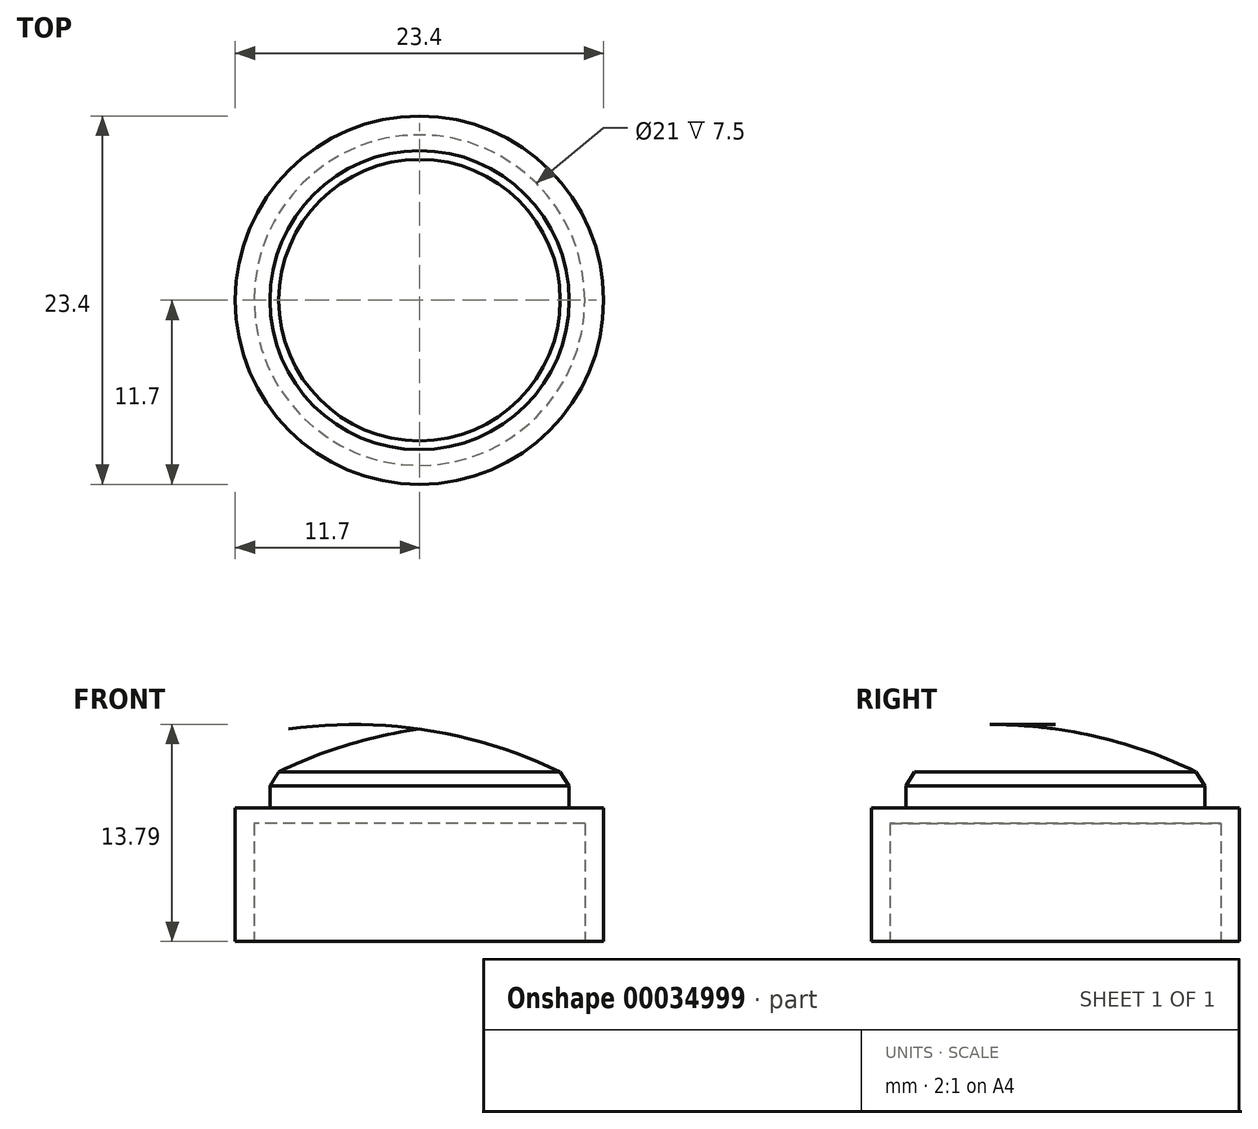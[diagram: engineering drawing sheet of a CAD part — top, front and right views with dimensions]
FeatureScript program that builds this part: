
annotation { "Feature Type Name" : "Feature", "Feature Type Description" : "" }
export const myFeature = defineFeature(function(context is Context, id is Id, definition is map)
    precondition{}
    {
        {
            var Q0;
            Q0=qCreatedBy(makeId("Top.planeOp"),FACE);
            var sketch = newSketch(context, id + "F0", { "sketchPlane" : qUnion([Q0])});
            skCircle(sketch, "E0", {"center": v(0, 0) * mm, "radius": 11.7 * mm});
            skCircle(sketch, "E1", {"center": v(0, 0) * mm, "radius": 10.5 * mm});
            skSolve(sketch);
        }
        {
            var Q0;
            Q0=makeQuery(id+"F0.imprint","IMPRINT",FACE,{"disambiguationData":[TD([[makeQuery(id+"F0.imprint","IMPRINT",EDGE,{"derivedFrom":sQuery(id+"F0.wireOp",EDGE,"E0")}),1.0]])]});
            var Q1;
            Q1=makeQuery(id+"F0.imprint","IMPRINT",FACE,{"disambiguationData":[TD([[makeQuery(id+"F0.imprint","IMPRINT",EDGE,{"derivedFrom":sQuery(id+"F0.wireOp",EDGE,"E1")}),1.0]])]});
            var Q2;
            Q2=sQuery(id+"F0.wireOp",EDGE,"E0");
            extrude(context, id + "F1", {"entities" : qUnion([Q0, Q1]), "surfaceEntities" : qUnion([Q2]), "depth" : 8.5 * mm});
        }
        {
            var Q0;
            Q0=makeQuery(id+"F0.imprint","IMPRINT",FACE,{"disambiguationData":[TD([[makeQuery(id+"F0.imprint","IMPRINT",EDGE,{"derivedFrom":sQuery(id+"F0.wireOp",EDGE,"E1")}),1.0]])]});
            extrude(context, id + "F2", {"entities" : qUnion([Q0]), "operationType" : NewBodyOperationType.REMOVE, "depth" : 7.5 * mm});
        }
        {
            var Q0;
            Q0=makeQuery(id+"F1.opExtrude","CAP_FACE",FACE,{"disambiguationData":[OSD([sQuery(id+"F0.wireOp",EDGE,"E0")])],"isStart":false});
            var sketch = newSketch(context, id + "F3", { "sketchPlane" : qUnion([Q0])});
            skCircle(sketch, "E2", {"center": v(0, 0) * mm, "radius": 9.5 * mm});
            skSolve(sketch);
        }
        {
            var Q0;
            Q0=makeQuery(id+"F3.imprint","IMPRINT",FACE,{"disambiguationData":[TD([[makeQuery(id+"F3.imprint","IMPRINT",EDGE,{"derivedFrom":sQuery(id+"F3.wireOp",EDGE,"b6d1c2b3-00fd-435d-919e-db7ff6a15c5d.0")}),1.0]])]});
            var Q1;
            Q1=makeQuery(id+"F3.imprint","IMPRINT",FACE,{"disambiguationData":[TD([[makeQuery(id+"F3.imprint","IMPRINT",EDGE,{"derivedFrom":sQuery(id+"F3.wireOp",EDGE,"E2")}),1.0]])]});
            extrude(context, id + "F4", {"entities" : qUnion([Q0, Q1]), "operationType" : NewBodyOperationType.ADD, "depth" : 2 * mm});
        }
        {
            var Q0;
            Q0=qCreatedBy(makeId("Front.planeOp"),FACE);
            var sketch = newSketch(context, id + "F5", { "sketchPlane" : qUnion([Q0])});
            skLineSegment(sketch, "E3", {"start": v(0, 0) * mm, "end": v(0, 24.67) * mm, "construction": true});
            skLineSegment(sketch, "E4", {"start": v(0, 10.5) * mm, "end": v(0, 13.5) * mm});
            skArc(sketch, "E5", {"start": v(0, 13.5) * mm, "mid": v(-4.88, 12.4) * mm, "end": v(-9.5, 10.5) * mm});
            skLineSegment(sketch, "E6.0", {"start": v(-9.5, 10.5) * mm, "end": v(9.5, 10.5) * mm});
            skSolve(sketch);
        }
        {
            var Q0;
            {var subQ2=sQuery(id+"F5.wireOp",EDGE,"E4");Q0=makeQuery(id+"F5.imprint","IMPRINT",FACE,{"disambiguationData":[TD([[makeQuery(id+"F5.imprint","IMPRINT",EDGE,{"derivedFrom":subQ2}),1.0]])]});}
            var Q1;
            Q1=sQuery(id+"F5.wireOp",EDGE,"E3");
            revolve(context, id + "F6", {"operationType" : NewBodyOperationType.ADD, "entities" : qUnion([Q0]), "axis" : qUnion([Q1]), "revolveType" : RevolveType.FULL});
        }
        {
            var Q0;
            Q0=makeQuery(id+"F6.boolean.opBoolean","MERGE",EDGE,{"derivedFrom":[makeQuery(id+"F4.opExtrude","CAP_EDGE",EDGE,{"disambiguationData":[OSD([sQuery(id+"F3.wireOp",EDGE,"E2")])],"isStart":false}),makeQuery(id+"F6.opRevolve","SWEPT_EDGE",EDGE,{"disambiguationData":[OSD([sQuery(id+"F5.wireOp",EDGE,"E5"),sQuery(id+"F5.wireOp",EDGE,"E6.0")])]})]});
            chamfer(context, id + "F7", {"entities" : qUnion([Q0]), "width" : 1 * mm, "tangentPropagation" : true});
        }
    });
